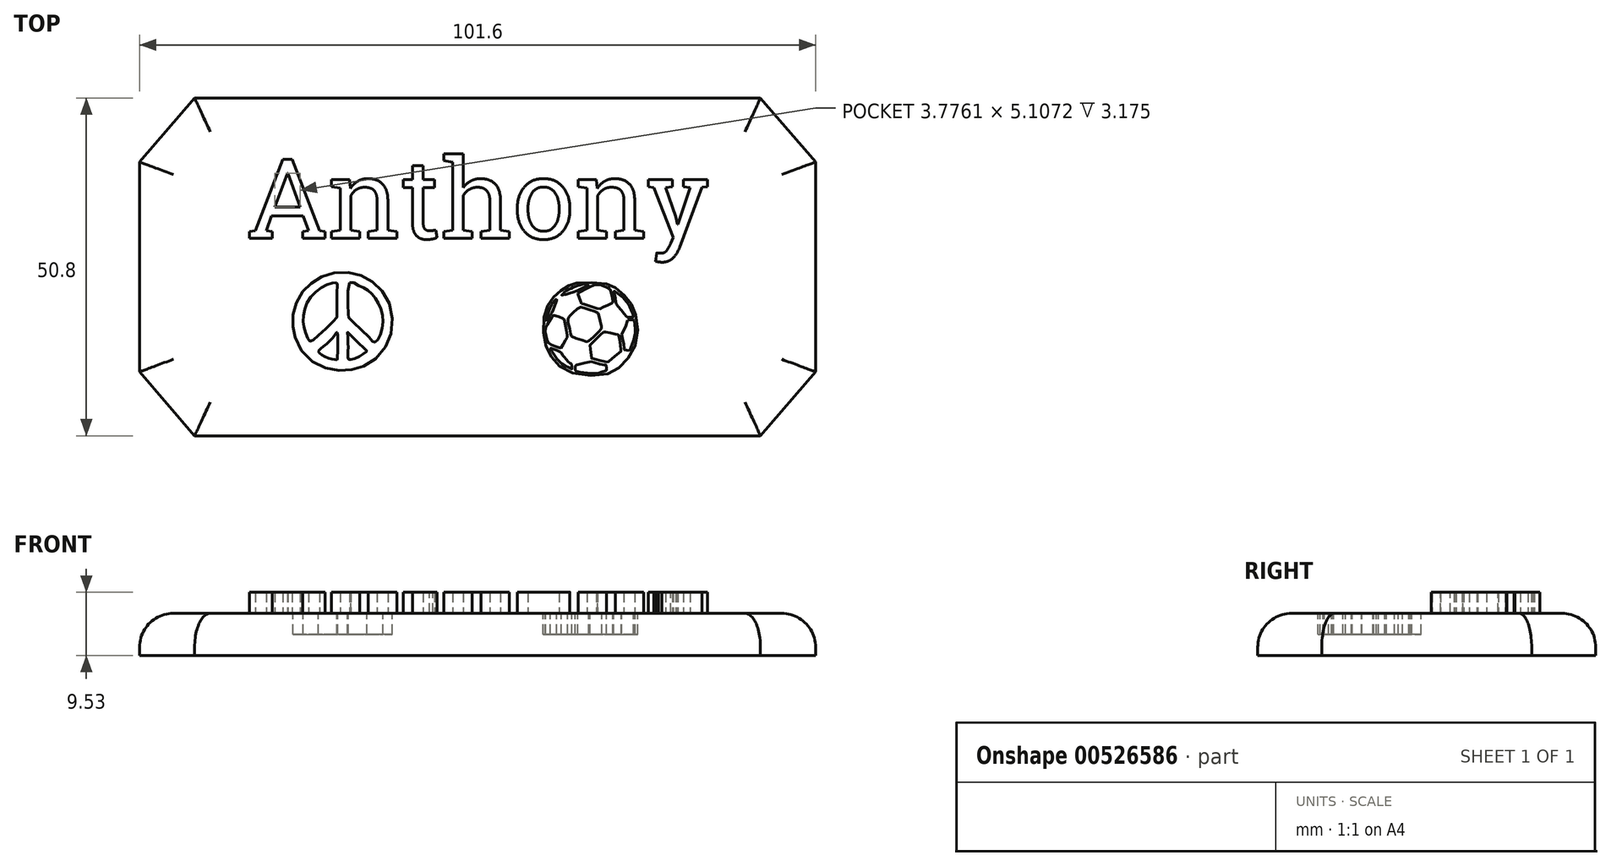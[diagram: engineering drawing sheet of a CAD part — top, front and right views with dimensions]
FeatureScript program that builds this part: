
annotation { "Feature Type Name" : "Feature", "Feature Type Description" : "" }
export const myFeature = defineFeature(function(context is Context, id is Id, definition is map)
    precondition{}
    {
        {
            var Q0;
            Q0=qCreatedBy(makeId("Top.planeOp"),FACE);
            var sketch = newSketch(context, id + "F0", { "sketchPlane" : qUnion([Q0])});
            skLineSegment(sketch, "E0", {"start": v(-40.32, 17.51) * mm, "end": v(44.72, 17.51) * mm});
            skLineSegment(sketch, "E1", {"start": v(44.72, 17.51) * mm, "end": v(53, 7.89) * mm});
            skLineSegment(sketch, "E2", {"start": v(53, 7.89) * mm, "end": v(53, -23.66) * mm});
            skLineSegment(sketch, "E3", {"start": v(53, -23.66) * mm, "end": v(44.72, -33.29) * mm});
            skLineSegment(sketch, "E4", {"start": v(44.72, -33.29) * mm, "end": v(-40.32, -33.29) * mm});
            skLineSegment(sketch, "E5", {"start": v(-40.32, -33.29) * mm, "end": v(-48.6, -23.66) * mm});
            skLineSegment(sketch, "E6", {"start": v(-48.6, -23.66) * mm, "end": v(-48.6, 7.89) * mm});
            skLineSegment(sketch, "E7", {"start": v(-48.6, 7.89) * mm, "end": v(-40.32, 17.51) * mm});
            skSolve(sketch);
        }
        {
            var Q0;
            Q0=makeQuery(id+"F0.imprint","IMPRINT",FACE,{"disambiguationData":[TD([[makeQuery(id+"F0.imprint","IMPRINT",EDGE,{"derivedFrom":sQuery(id+"F0.wireOp",EDGE,"E0")}),-1.0]])]});
            extrude(context, id + "F1", {"entities" : qUnion([Q0]), "depth" : 6.35 * mm, "offsetDistance" : 25.4 * mm});
        }
        {
            var Q0;
            Q0=makeQuery(id+"F1.opExtrude","CAP_EDGE",EDGE,{"disambiguationData":[OSD([sQuery(id+"F0.wireOp",EDGE,"E7")])],"isStart":false});
            var Q1;
            Q1=makeQuery(id+"F1.opExtrude","CAP_FACE",FACE,{"disambiguationData":[OSD([sQuery(id+"F0.wireOp",EDGE,"E0"),sQuery(id+"F0.wireOp",EDGE,"E1"),sQuery(id+"F0.wireOp",EDGE,"E2"),sQuery(id+"F0.wireOp",EDGE,"E3"),sQuery(id+"F0.wireOp",EDGE,"E4"),sQuery(id+"F0.wireOp",EDGE,"E5"),sQuery(id+"F0.wireOp",EDGE,"E6"),sQuery(id+"F0.wireOp",EDGE,"E7")])],"isStart":false});
            fillet(context, id + "F2", {"entities" : qUnion([Q0, Q1]), "radius" : 5.08 * mm, "tangentPropagation" : true, "allowEdgeOverflow" : false});
        }
        {
            var Q0;
            Q0=makeQuery(id+"F1.opExtrude","CAP_FACE",FACE,{"disambiguationData":[OSD([sQuery(id+"F0.wireOp",EDGE,"E0"),sQuery(id+"F0.wireOp",EDGE,"E1"),sQuery(id+"F0.wireOp",EDGE,"E2"),sQuery(id+"F0.wireOp",EDGE,"E3"),sQuery(id+"F0.wireOp",EDGE,"E4"),sQuery(id+"F0.wireOp",EDGE,"E5"),sQuery(id+"F0.wireOp",EDGE,"E6"),sQuery(id+"F0.wireOp",EDGE,"E7")])],"isStart":false});
            var sketch = newSketch(context, id + "F3", { "sketchPlane" : qUnion([Q0])});
            skText(sketch, "E8", { "text": "Anthony", "fontName": "RobotoSlab-Regular.ttf"});
            const initialGuessF3  = {"E8": [-0.03253, -0.00361, 1, 0, 0.01205]};
            skSetInitialGuess(sketch, initialGuessF3);
            skSolve(sketch);
        }
        {
            var Q0;
            Q0 = qSketchRegion(id + "F3", true);
            extrude(context, id + "F4", {"entities" : qUnion([Q0]), "operationType" : NewBodyOperationType.ADD, "depth" : 3.17 * mm, "offsetDistance" : 25.4 * mm});
        }
        {
            var Q0;
            {var subQ0=sQuery(id+"F0.wireOp",EDGE,"E3");var subQ1=sQuery(id+"F0.wireOp",EDGE,"E2");var subQ2=sQuery(id+"F0.wireOp",EDGE,"E1");var subQ3=sQuery(id+"F0.wireOp",EDGE,"E0");var subQ4=sQuery(id+"F0.wireOp",EDGE,"E4");var subQ5=sQuery(id+"F0.wireOp",EDGE,"E5");var subQ6=sQuery(id+"F0.wireOp",EDGE,"E6");var subQ7=sQuery(id+"F0.wireOp",EDGE,"E7");Q0=makeQuery(id+"F4.boolean.opBoolean","SPLIT",FACE,{"disambiguationData":[TD([makeQuery(id+"F2.opFillet","BLEND_FACE",FACE,{"disambiguationData":[OSD([subQ3])]})])],"derivedFrom":makeQuery(id+"F1.opExtrude","CAP_FACE",FACE,{"disambiguationData":[OSD([subQ3,subQ2,subQ1,subQ0,subQ4,subQ5,subQ6,subQ7])],"isStart":false})});}
            var sketch = newSketch(context, id + "F5", { "sketchPlane" : qUnion([Q0])});
            skFitSpline(sketch, "E9", {"points": [v(-19.38, -8.8) * mm, v(-21.27, -9.36) * mm, v(-22.93, -10.46) * mm, v(-24.1, -11.63) * mm, v(-25.08, -13.42) * mm, v(-25.53, -15.28) * mm, v(-25.53, -16.94) * mm, v(-25.27, -18.33) * mm, v(-24.07, -20.7) * mm, v(-21.89, -22.53) * mm, v(-19.64, -23.34) * mm, v(-17.4, -23.44) * mm, v(-15.61, -23.05) * mm, v(-13.66, -22.1) * mm, v(-11.68, -20.03) * mm, v(-10.73, -17.65) * mm, v(-10.7, -14.76) * mm, v(-11.64, -12.19) * mm, v(-13.1, -10.5) * mm, v(-14.96, -9.36) * mm, v(-16.91, -8.77) * mm, v(-19.38, -8.8) * mm]});
            skFitSpline(sketch, "E10", {"points": [v(-18.9, -10.56) * mm, v(-18.93, -10.3) * mm, v(-19.77, -10.33) * mm, v(-21.53, -11.18) * mm, v(-23.25, -12.97) * mm, v(-23.94, -15.08) * mm, v(-23.9, -16.84) * mm, v(-23.35, -18.53) * mm, v(-22.93, -19.08) * mm, v(-21.8, -18.27) * mm, v(-18.93, -15.47) * mm, v(-18.9, -15.18) * mm, v(-18.9, -10.56) * mm]});
            skFitSpline(sketch, "E11", {"points": [v(-17.04, -10.27) * mm, v(-16, -10.5) * mm, v(-14.73, -11.11) * mm, v(-13.56, -12.09) * mm, v(-12.68, -13.42) * mm, v(-12.07, -15.4) * mm, v(-12.26, -17.59) * mm, v(-12.98, -19.05) * mm, v(-13.43, -19.21) * mm, v(-14.08, -18.5) * mm, v(-17.2, -15.47) * mm, v(-17.2, -15.34) * mm, v(-17.04, -10.27) * mm]});
            skFitSpline(sketch, "E12", {"points": [v(-18.9, -17.72) * mm, v(-18.86, -21.65) * mm, v(-18.93, -21.85) * mm, v(-20.36, -21.55) * mm, v(-21.7, -20.68) * mm, v(-21.3, -20.12) * mm, v(-19.29, -18.2) * mm, v(-18.9, -17.72) * mm]});
            skFitSpline(sketch, "E13", {"points": [v(-17.08, -17.94) * mm, v(-14.5, -20.45) * mm, v(-14.47, -20.61) * mm, v(-17.01, -21.85) * mm, v(-17.27, -20.94) * mm, v(-17.3, -18.37) * mm, v(-17.34, -17.68) * mm, v(-17.08, -17.94) * mm]});
            skSolve(sketch);
        }
        {
            var Q0;
            Q0=makeQuery(id+"F5.imprint","IMPRINT",FACE,{"disambiguationData":[TD([[makeQuery(id+"F5.imprint","IMPRINT",EDGE,{"derivedFrom":sQuery(id+"F5.wireOp",EDGE,"E9")}),1.0]])]});
            extrude(context, id + "F6", {"entities" : qUnion([Q0]), "operationType" : NewBodyOperationType.REMOVE, "oppositeDirection" : true, "depth" : 3.17 * mm, "offsetDistance" : 25.4 * mm});
        }
        {
            var Q0;
            {var subQ51=sQuery(id+"F0.wireOp",EDGE,"E3");var subQ56=sQuery(id+"F0.wireOp",EDGE,"E2");var subQ62=sQuery(id+"F0.wireOp",EDGE,"E1");var subQ68=sQuery(id+"F0.wireOp",EDGE,"E0");var subQ69=makeQuery(id+"F2.opFillet","BLEND_FACE",FACE,{"disambiguationData":[OSD([subQ68])]});var subQ74=sQuery(id+"F0.wireOp",EDGE,"E4");var subQ78=sQuery(id+"F0.wireOp",EDGE,"E5");var subQ83=sQuery(id+"F0.wireOp",EDGE,"E6");var subQ87=sQuery(id+"F0.wireOp",EDGE,"E7");Q0=makeQuery(id+"F6.boolean.opBoolean","SPLIT",FACE,{"disambiguationData":[TD([subQ69])],"derivedFrom":makeQuery(id+"F4.boolean.opBoolean","SPLIT",FACE,{"disambiguationData":[TD([subQ69])],"derivedFrom":makeQuery(id+"F1.opExtrude","CAP_FACE",FACE,{"disambiguationData":[OSD([subQ68,subQ62,subQ56,subQ51,subQ74,subQ78,subQ83,subQ87])],"isStart":false})})});}
            var sketch = newSketch(context, id + "F7", { "sketchPlane" : qUnion([Q0])});
            skFitSpline(sketch, "E14", {"points": [v(17.07, -10.34) * mm, v(15.93, -10.7) * mm, v(14.5, -11.6) * mm, v(13.3, -12.84) * mm, v(12.32, -14.86) * mm, v(12.25, -19.06) * mm, v(13.42, -21.53) * mm, v(15.76, -23.58) * mm, v(21.4, -24.03) * mm, v(23.96, -22.57) * mm, v(26.01, -19.35) * mm, v(25.95, -15) * mm, v(24.94, -12.9) * mm, v(22.99, -11.09) * mm, v(21.4, -10.37) * mm, v(17.07, -10.34) * mm]});
            skPoint(sketch, "E15.0.internal.snap0", {"position": v(19.12, -10.02) * mm});
            skPoint(sketch, "E15.1.internal.snap0", {"position": v(19.12, -10.02) * mm});
            skFitSpline(sketch, "E16", {"points": [v(14.1, -12.73) * mm, v(13.44, -13.41) * mm, v(12.86, -14.62) * mm, v(12.47, -15.95) * mm, v(12.95, -15.36) * mm, v(13.31, -14.84) * mm, v(14.1, -12.73) * mm]});
            skFitSpline(sketch, "E17", {"points": [v(18.9, -10.49) * mm, v(16.86, -11.56) * mm, v(14.8, -12.14) * mm, v(14.84, -12.11) * mm, v(15.46, -11.53) * mm, v(16.76, -10.9) * mm, v(17.93, -10.52) * mm, v(18.9, -10.49) * mm]});
            skFitSpline(sketch, "E18", {"points": [v(18.48, -11.2) * mm, v(17.26, -11.83) * mm, v(17.25, -11.88) * mm, v(17.8, -13.36) * mm, v(17.95, -13.43) * mm, v(20.39, -14.17) * mm, v(20.83, -14.05) * mm, v(22.45, -13.33) * mm, v(22.55, -13.16) * mm, v(22.2, -11.44) * mm, v(22.05, -11.22) * mm, v(21.48, -10.88) * mm, v(20.69, -10.63) * mm, v(20.05, -10.55) * mm, v(18.48, -11.2) * mm]});
            skFitSpline(sketch, "E19", {"points": [v(23.8, -12.26) * mm, v(24.16, -12.6) * mm, v(24.8, -13.42) * mm, v(25.26, -14.31) * mm, v(25.6, -15.44) * mm, v(25.37, -15.44) * mm, v(24.67, -15.45) * mm, v(24.47, -15.23) * mm, v(23.1, -13.5) * mm, v(23, -13.2) * mm, v(22.72, -11.62) * mm, v(22.7, -11.49) * mm, v(23.8, -12.26) * mm]});
            skFitSpline(sketch, "E20", {"points": [v(24.72, -15.88) * mm, v(25.69, -15.87) * mm, v(25.74, -15.88) * mm, v(25.88, -17.39) * mm, v(25.7, -18.74) * mm, v(25.25, -20) * mm, v(25.03, -20.44) * mm, v(24.86, -20.45) * mm, v(24.3, -20.37) * mm, v(24.24, -20.1) * mm, v(23.88, -18.02) * mm, v(23.97, -17.81) * mm, v(24.66, -16.07) * mm, v(24.72, -15.88) * mm]});
            skFitSpline(sketch, "E21", {"points": [v(21.46, -17.66) * mm, v(23.18, -18.06) * mm, v(23.35, -18.09) * mm, v(23.47, -18.32) * mm, v(23.77, -20.4) * mm, v(23.7, -20.65) * mm, v(21.9, -22.12) * mm, v(21.8, -22.2) * mm, v(19.37, -21.64) * mm, v(19.33, -21.59) * mm, v(19.12, -19.67) * mm, v(19.25, -19.48) * mm, v(21.12, -17.72) * mm, v(21.46, -17.66) * mm]});
            skFitSpline(sketch, "E22", {"points": [v(16.9, -23.07) * mm, v(16.91, -22.78) * mm, v(17.13, -22.62) * mm, v(19.06, -22.15) * mm, v(19.35, -22.16) * mm, v(21.42, -22.64) * mm, v(21.55, -22.66) * mm, v(21.56, -23.45) * mm, v(21.47, -23.5) * mm, v(20.57, -23.77) * mm, v(19.12, -23.89) * mm, v(17.74, -23.74) * mm, v(16.9, -23.46) * mm, v(16.9, -23.07) * mm]});
            skFitSpline(sketch, "E23", {"points": [v(14.58, -20.63) * mm, v(14.94, -21.07) * mm, v(15.53, -21.76) * mm, v(16.11, -22.37) * mm, v(16.35, -22.53) * mm, v(16.36, -23.26) * mm, v(16.32, -23.25) * mm, v(15.08, -22.58) * mm, v(14.1, -21.66) * mm, v(13.44, -20.7) * mm, v(13.16, -20.1) * mm, v(13.22, -20.1) * mm, v(14.58, -20.63) * mm]});
            skFitSpline(sketch, "E24", {"points": [v(18.2, -14.07) * mm, v(20.12, -14.7) * mm, v(20.4, -15.07) * mm, v(20.82, -16.9) * mm, v(20.8, -17.22) * mm, v(18.86, -19.06) * mm, v(18.5, -19.09) * mm, v(16.41, -18.36) * mm, v(16.17, -17.86) * mm, v(15.76, -15.82) * mm, v(16, -15.37) * mm, v(17.5, -13.99) * mm, v(18.2, -14.07) * mm]});
            skFitSpline(sketch, "E25", {"points": [v(13.02, -16) * mm, v(13.56, -15.2) * mm, v(13.74, -15.16) * mm, v(15.13, -15.67) * mm, v(15.23, -15.87) * mm, v(15.72, -18.33) * mm, v(15.63, -18.58) * mm, v(14.69, -20.08) * mm, v(14.5, -20.06) * mm, v(13.02, -19.45) * mm, v(12.6, -18.7) * mm, v(12.4, -17.3) * mm, v(13.02, -16) * mm]});
            skSolve(sketch);
        }
        {
            var Q0;
            Q0=makeQuery(id+"F7.imprint","IMPRINT",FACE,{"disambiguationData":[TD([[makeQuery(id+"F7.imprint","IMPRINT",EDGE,{"derivedFrom":sQuery(id+"F7.wireOp",EDGE,"E14")}),1.0]])]});
            extrude(context, id + "F8", {"entities" : qUnion([Q0]), "operationType" : NewBodyOperationType.REMOVE, "oppositeDirection" : true, "depth" : 3.17 * mm, "offsetDistance" : 25.4 * mm});
        }
    });
